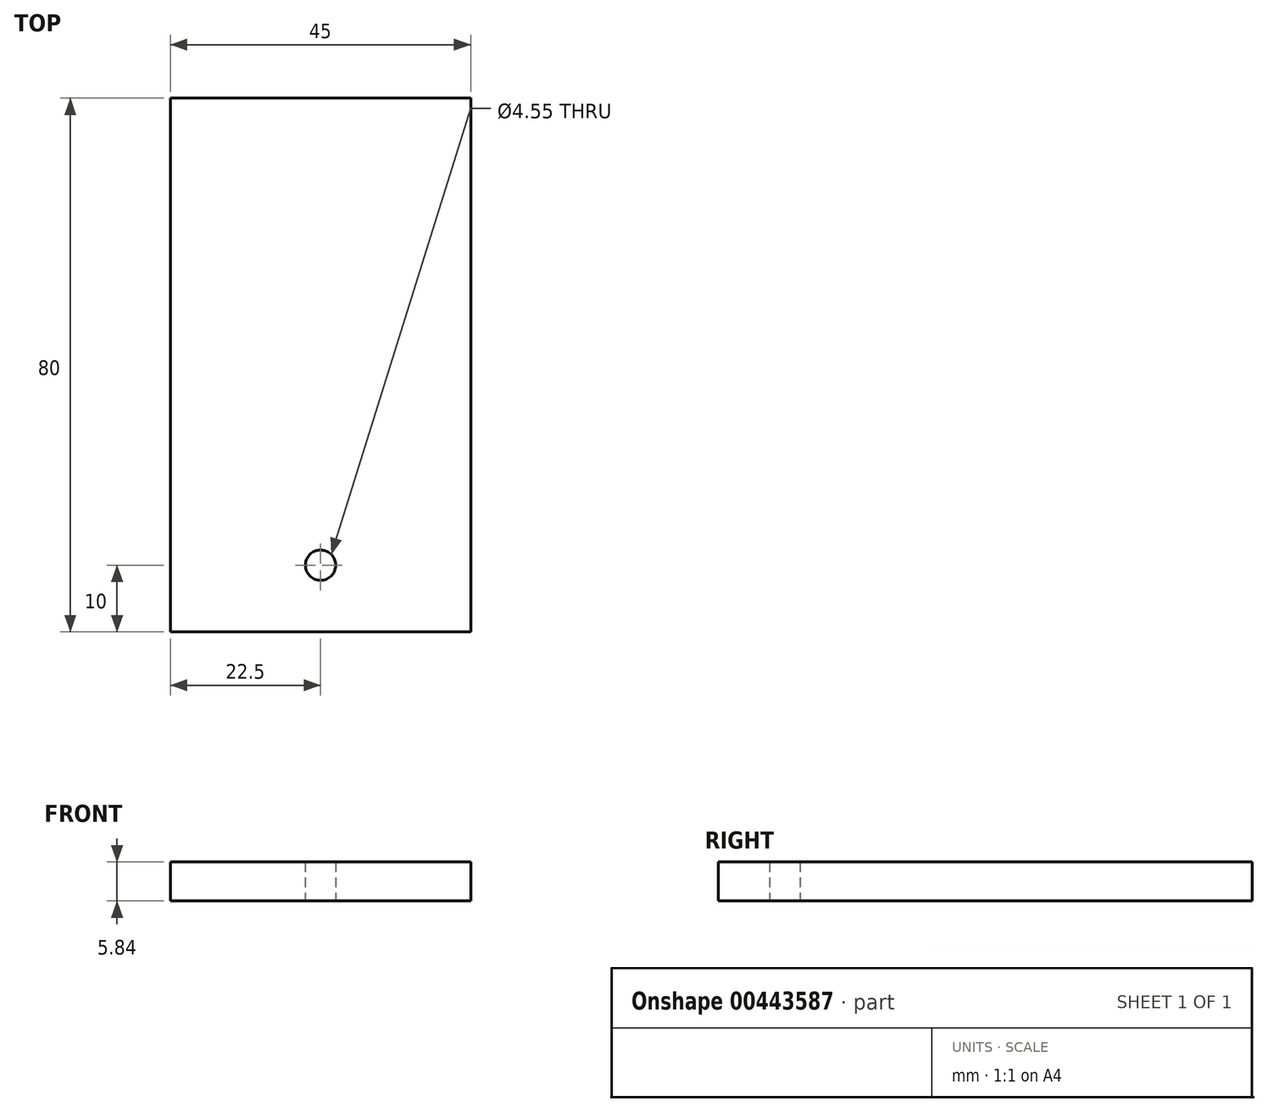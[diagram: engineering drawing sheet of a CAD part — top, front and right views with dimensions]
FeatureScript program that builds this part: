
annotation { "Feature Type Name" : "Feature", "Feature Type Description" : "" }
export const myFeature = defineFeature(function(context is Context, id is Id, definition is map)
    precondition{}
    {
        {
            var Q0;
            Q0=qCreatedBy(makeId("Top.planeOp"),FACE);
            var sketch = newSketch(context, id + "F0", { "sketchPlane" : qUnion([Q0])});
            skLineSegment(sketch, "E0.bottom", {"start": v(0, 0) * mm, "end": v(-45, 0) * mm});
            skLineSegment(sketch, "E0.top", {"start": v(0, 80) * mm, "end": v(-45, 80) * mm});
            skLineSegment(sketch, "E0.left", {"start": v(0, 0) * mm, "end": v(0, 80) * mm});
            skLineSegment(sketch, "E0.right", {"start": v(-45, 0) * mm, "end": v(-45, 80) * mm});
            skCircle(sketch, "E1", {"center": v(-22.5, 10) * mm, "radius": 2.27 * mm});
            skPoint(sketch, "E2", {"position": v(-45, 9.83) * mm});
            skPoint(sketch, "E3", {"position": v(0, 10.17) * mm});
            skSolve(sketch);
        }
        {
            var Q0;
            Q0=qSketchRegion(id+"F0",true);
            extrude(context, id + "F1", {"entities" : qUnion([Q0]), "depth" : 5.84 * mm});
        }
    });
